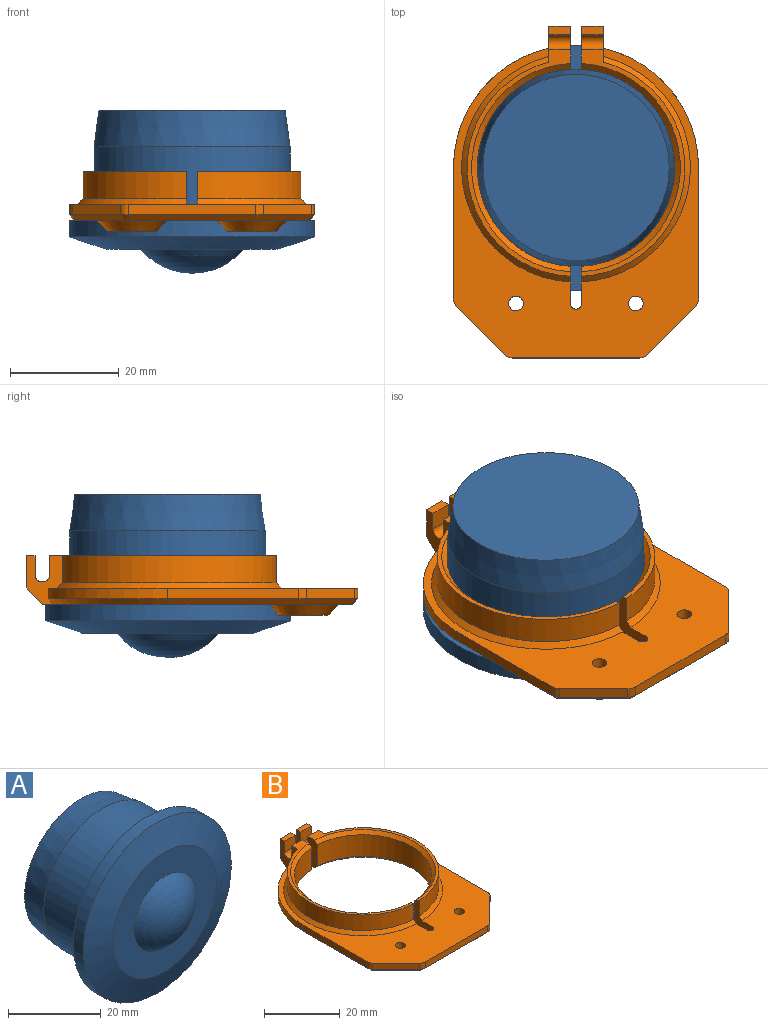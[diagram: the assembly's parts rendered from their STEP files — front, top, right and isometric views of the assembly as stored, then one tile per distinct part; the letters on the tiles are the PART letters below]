
ASSEMBLY  parts=2 mates=1
PART A: 8 faces, bbox 45x30x45 mm
  f0: cylinder r=18mm len=36mm, axis (0,1,0), area 1523mm2, adj f1,f7
  f1: cone r=17.55mm half-angle=7.6deg, axis (0,-1,0), area 749.1mm2, adj f0,f6
  f2: cone r=19.12mm half-angle=71.6deg, axis (0,1,0), area 855mm2, adj f3,f5
  f3: cylinder r=22.5mm len=45mm, axis (0,1,0), area 431.2mm2, adj f2,f7
  f4: sphere r=12mm, area 339.3mm2, adj f5
  f5: plane 31.5x31.5mm, normal (0,-1,0), area 503.6mm2, adj f2,f4
  f6: plane 34.2x34.2mm, normal (0,1,0), area 918.6mm2, adj f1
  f7: plane 45x45mm, normal (0,1,0), area 572.6mm2, adj f0,f3
PART B: 77 faces, bbox 45x60.9x11 mm
  f0: cone r=22mm half-angle=45deg, axis (0,0,1), area 41.7mm2, adj f1,f21,f22,f39
  f1: plane 24.1x1mm, normal (0.71,0,-0.71), area 34.1mm2, adj f0,f2,f20,f22
  f2: cone r=1.5mm half-angle=45deg, axis (0,0,1), area 1.7mm2, adj f1,f3,f19,f22
  f3: plane 9.54x9.54mm, normal (0.5,-0.5,-0.71), area 17.7mm2, adj f2,f4,f18,f22
  f4: cone r=1.5mm half-angle=45deg, axis (0,0,1), area 1.7mm2, adj f3,f5,f17,f22
  f5: plane 23.34x1mm, normal (0,-0.71,-0.71), area 33mm2, adj f4,f6,f16,f22
  f6: cone r=1.5mm half-angle=45deg, axis (0,0,1), area 1.7mm2, adj f5,f7,f15,f22
  f7: plane 9.54x9.54mm, normal (-0.5,-0.5,-0.71), area 17.7mm2, adj f6,f8,f14,f22
  f8: cone r=1.5mm half-angle=45deg, axis (0,0,1), area 1.7mm2, adj f7,f9,f13,f22
  f9: plane 24.1x1mm, normal (-0.71,0,-0.71), area 34.1mm2, adj f8,f10,f12,f22
  f10: cone r=22mm half-angle=45deg, axis (0,0,1), area 41.7mm2, adj f9,f11,f22,f42
  f11: cylinder r=22.5mm len=21.94mm, axis (0,0,1), area 59.1mm2, adj f10,f12,f23,f42
  f12: plane 24.1x1.95mm, normal (-1,0,0), area 47mm2, adj f9,f11,f13,f23
  f13: cylinder r=2mm len=1.95mm, axis (0,0,-1), area 3.1mm2, adj f8,f12,f14,f23
  f14: plane 8.83x8.83mm, normal (-0.71,-0.71,0), area 24.3mm2, adj f7,f13,f15,f23
  f15: cylinder r=2mm len=1.95mm, axis (0,0,1), area 3.1mm2, adj f6,f14,f16,f23
  f16: plane 23.34x1.95mm, normal (0,-1,0), area 45.5mm2, adj f5,f15,f17,f23
  f17: cylinder r=2mm len=1.95mm, axis (0,0,-1), area 3.1mm2, adj f4,f16,f18,f23
  f18: plane 8.83x8.83mm, normal (0.71,-0.71,0), area 24.3mm2, adj f3,f17,f19,f23
  f19: cylinder r=2mm len=1.95mm, axis (0,0,1), area 3.1mm2, adj f2,f18,f20,f23
  f20: plane 24.1x1.95mm, normal (1,0,0), area 47mm2, adj f1,f19,f21,f23
  f21: cylinder r=22.5mm len=21.94mm, axis (0,0,1), area 59.1mm2, adj f0,f20,f23,f39
  f22: plane 56.93x43mm, normal (0,0,-1), area 702.4mm2, adj f0,f1,f2,f3,f4,f5,f6,f7
  f23: plane 56.87x45mm, normal (0,0,1), area 845.1mm2, adj f11,f12,f13,f14,f15,f16,f17,f18
  f24: plane 8.97x6.9mm, normal (1,0,0), area 30.9mm2, adj f22,f23,f25,f27,f28,f30,f32,f34
  f25: cylinder r=1mm len=2.95mm, axis (0,0,1), area 9.3mm2, adj f22,f23,f24,f26
  f26: plane 8.97x6.9mm, normal (-1,0,0), area 30.9mm2, adj f22,f23,f25,f29,f31,f33,f35,f37
  f27: cone r=18.65mm half-angle=45deg, axis (0,0,-1), area 80mm2, adj f22,f24,f28,f53
  f28: cylinder r=18.15mm len=36.25mm, axis (0,0,1), area 382.4mm2, adj f24,f27,f30,f53
  f29: cylinder r=18.15mm len=36.25mm, axis (0,0,1), area 382.4mm2, adj f26,f31,f49,f54
  f30: cone r=18.65mm half-angle=45deg, axis (0,0,1), area 80mm2, adj f24,f28,f32,f53
  f31: cone r=18.65mm half-angle=45deg, axis (0,0,1), area 80mm2, adj f26,f29,f33,f49
  f32: plane 41.63x19mm, normal (0,0,1), area 58.2mm2, adj f24,f30,f34,f42,f43,f53
  f33: plane 41.63x19mm, normal (0,0,1), area 58.2mm2, adj f26,f31,f35,f39,f48,f49
  f34: cylinder r=20mm len=39.34mm, axis (0,0,1), area 283.9mm2, adj f24,f32,f36,f42
  f35: cylinder r=20mm len=39.34mm, axis (0,0,1), area 283.9mm2, adj f26,f33,f37,f39
  f36: cone r=20.5mm half-angle=45deg, axis (0,0,-1), area 82.5mm2, adj f23,f24,f34,f42
  f37: cone r=20.5mm half-angle=45deg, axis (0,0,-1), area 82.5mm2, adj f23,f26,f35,f39
  f38: plane 4x3mm, normal (0,0.71,-0.71), area 17mm2, adj f22,f39,f49,f52
  f39: plane 8.97x6.65mm, normal (1,0,0), area 35mm2, adj f0,f21,f22,f23,f33,f35,f37,f38
  f40: plane 4x3mm, normal (0,0.71,-0.71), area 17mm2, adj f22,f41,f42,f53
  f41: plane 5.95x4mm, normal (0,1,0), area 23.8mm2, adj f40,f42,f50,f53
  f42: plane 8.97x6.65mm, normal (-1,0,0), area 35mm2, adj f10,f11,f22,f23,f32,f34,f36,f40
  f43: plane 4x3.5mm, normal (0,1,0), area 14mm2, adj f32,f42,f44,f53
  f44: cylinder r=1.35mm len=4mm, axis (1,0,0), area 17mm2, adj f42,f43,f46,f53
  f45: cylinder r=1.35mm len=4mm, axis (1,0,0), area 17mm2, adj f39,f47,f48,f49
  f46: plane 4x3.5mm, normal (0,-1,0), area 14mm2, adj f42,f44,f50,f53
  f47: plane 4x3.5mm, normal (0,-1,0), area 14mm2, adj f39,f45,f49,f51
  f48: plane 4x3.5mm, normal (0,1,0), area 14mm2, adj f33,f39,f45,f49
  f49: plane 8.97x7.9mm, normal (-1,0,0), area 52.7mm2, adj f22,f29,f31,f33,f38,f45,f47,f48
  f50: plane 4x1.65mm, normal (0,0,1), area 6.6mm2, adj f41,f42,f46,f53
  f51: plane 4x1.65mm, normal (0,0,1), area 6.6mm2, adj f39,f47,f49,f52
  f52: plane 5.95x4mm, normal (0,1,0), area 23.8mm2, adj f38,f39,f49,f51
  f53: plane 8.97x7.9mm, normal (1,0,0), area 52.7mm2, adj f22,f27,f28,f30,f32,f40,f41,f43
  f54: cone r=18.65mm half-angle=45deg, axis (0,0,-1), area 80mm2, adj f22,f26,f29,f49
  f55: cylinder r=23mm len=8.23mm, axis (0,0,-1), area 11.8mm2, adj f22,f58,f59
  f56: cylinder r=23mm len=8.23mm, axis (0,0,-1), area 11.8mm2, adj f22,f57,f60
  f57: cone r=5.5mm half-angle=45deg, axis (0,0,1), area 80.6mm2, adj f22,f56,f60
  f58: cone r=5.5mm half-angle=45deg, axis (0,0,1), area 80.6mm2, adj f22,f55,f59
  f59: plane 9x9mm, normal (0,0,-1), area 39.7mm2, adj f55,f58,f68,f69,f70,f71,f72,f73
  f60: plane 9x9mm, normal (0,0,-1), area 39.7mm2, adj f56,f57,f61,f62,f63,f64,f65,f66
  f61: plane 3x2.6mm, normal (0.87,-0.5,0), area 9mm2, adj f60,f62,f66,f67
  f62: plane 3x3mm, normal (0,-1,0), area 9mm2, adj f60,f61,f63,f67
  f63: plane 3x2.6mm, normal (-0.87,-0.5,0), area 9mm2, adj f60,f62,f64,f67
  f64: plane 3x2.6mm, normal (-0.87,0.5,0), area 9mm2, adj f60,f63,f65,f67
  f65: plane 3x3mm, normal (0,1,0), area 9mm2, adj f60,f64,f66,f67
  f66: plane 3x2.6mm, normal (0.87,0.5,0), area 9mm2, adj f60,f61,f65,f67
  f67: plane 6x5.2mm, normal (0,0,-1), area 17.7mm2, adj f61,f62,f63,f64,f65,f66,f75
  f68: plane 3x2.6mm, normal (-0.87,0.5,0), area 9mm2, adj f59,f69,f73,f74
  f69: plane 3x3mm, normal (0,1,0), area 9mm2, adj f59,f68,f70,f74
  f70: plane 3x2.6mm, normal (0.87,0.5,0), area 9mm2, adj f59,f69,f71,f74
  f71: plane 3x2.6mm, normal (0.87,-0.5,0), area 9mm2, adj f59,f70,f72,f74
  f72: plane 3x3mm, normal (0,-1,0), area 9mm2, adj f59,f71,f73,f74
  f73: plane 3x2.6mm, normal (-0.87,-0.5,0), area 9mm2, adj f59,f68,f72,f74
  f74: plane 6x5.2mm, normal (0,0,-1), area 17.7mm2, adj f68,f69,f70,f71,f72,f73,f76
  f75: cylinder r=1.35mm len=2.7mm, axis (0,0,1), area 16.5mm2, adj f23,f67
  f76: cylinder r=1.35mm len=2.7mm, axis (0,0,1), area 16.5mm2, adj f23,f74
PLACE A rot(axis=(1,0,0),90deg) t=(30.61,18.54,-8.87)mm
PLACE B t=(30.61,18.54,-8.87)mm fixed
MATE fastened A.f0 <-> B.f0  axis (0,0,1) through (30.61,18.54,-8.87)mm
